# Revit family: fire_rinnai_ember600_framing
name_source: partatom
category: Specialty Equipment
revit_build: Autodesk Revit 2017 (Build: 20170816_0615(x64)
units: mm (PartAtom-declared; Revit-internal decimal feet)

## family parameters
Always vertical = Yes
Cut with Voids When Loaded = Yes
Host = Wall
Part Type = Normal
Room Calculation Point = No
Round Connector Dimension = Use Diameter
Shared = No

## types (2) — shared parameters
Manufacturer = Rinnai NZ Ltd
Model = Ember 600
Type Comments = Ember 600
URL = www.rinnai.co.nz
_fire_clearceiling = 1000 mm  [stored 3.28084 ft]
_fire_cleardepth = 1000 mm  [stored 3.28084 ft]
_fire_clearheight = 400 mm  [stored 1.31234 ft]
_fire_side_clearance = 400 mm  [stored 1.31234 ft]
_fire_width = 590 mm  [stored 1.9357 ft]
_fire_window_top = 570 mm  [stored 1.87008 ft]
_fire_window_width = 540 mm  [stored 1.77165 ft]
_opening_depth = 400 mm  [stored 1.31234 ft]
_opening_height = 700 mm  [stored 2.29659 ft]
_opening_width = 700 mm  [stored 2.29659 ft]
_rinnai_product = Fires
clearance = 10 mm  [stored 0.0328084 ft]
m_body = Rinnai Body
m_cowl = Rinnai Cowl
m_flames = Rinnai Flames
m_flue = Rinnai Flue
m_frame = Rinnai Black Frame
m_gas = Rinnai Gas
m_glass = Rinnai_fireglass
m_plinth = <By Category>
m_rinnai = Rinnai_logo
v_fireplace = Yes
zero-valued in all types: _clearance_offset, _fire_opening_offset, opening floor offset

## per-type parameters (varying)
| type | Description | Front frame | _fire_top | _fire_wall_lining |
| 4 sided frame | Rinnai Ember 600 Framing 4 sided front | ember600_mod : ember600_framing_4sided | 580 mm  [stored 1.90289 ft] | 10 mm  [stored 0.0328084 ft] |
| 3 sided frame | Rinnai Ember 600 Framing 3 sided front | ember600_mod : ember600_framing_3sided | 585 mm  [stored 1.91929 ft] | 20 mm |

note: [stored X ft] marks values corroborated as IEEE doubles in the binary element streams (Revit-internal decimal feet)

## geometry (parser evidence)
native form markers: Sweep x15
no freeform markers — native parametric forms only
